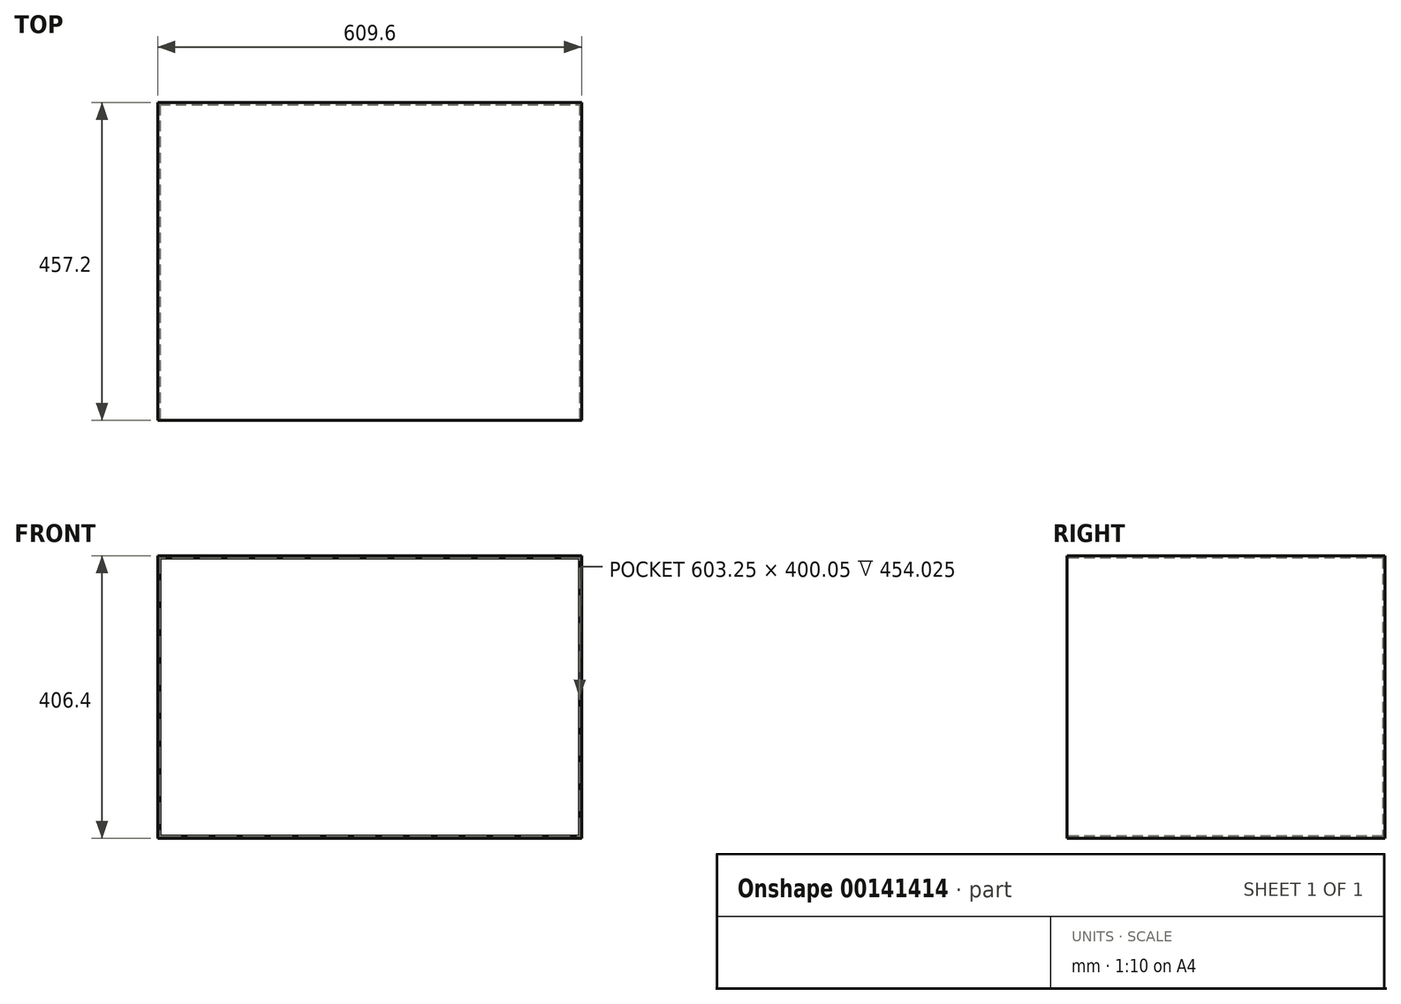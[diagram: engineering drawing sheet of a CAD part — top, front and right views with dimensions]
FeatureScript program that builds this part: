
annotation { "Feature Type Name" : "Feature", "Feature Type Description" : "" }
export const myFeature = defineFeature(function(context is Context, id is Id, definition is map)
    precondition{}
    {
        {
            var Q0;
            Q0=qCreatedBy(makeId("Top.planeOp"),FACE);
            var sketch = newSketch(context, id + "F0", { "sketchPlane" : qUnion([Q0])});
            skLineSegment(sketch, "E0.bottom", {"start": v(-304.8, 228.6) * mm, "end": v(304.8, 228.6) * mm});
            skLineSegment(sketch, "E0.top", {"start": v(-304.8, -228.6) * mm, "end": v(304.8, -228.6) * mm});
            skLineSegment(sketch, "E0.left", {"start": v(-304.8, 228.6) * mm, "end": v(-304.8, -228.6) * mm});
            skLineSegment(sketch, "E0.right", {"start": v(304.8, 228.6) * mm, "end": v(304.8, -228.6) * mm});
            skPoint(sketch, "E0.middle", {"position": v(0, 0) * mm});
            skSolve(sketch);
        }
        {
            var Q0;
            Q0 = qSketchRegion(id + "F0", true);
            extrude(context, id + "F1", {"entities" : qUnion([Q0]), "depth" : 406.4 * mm});
        }
        {
            var Q0;
            Q0=makeQuery(id+"F1.opExtrude","SWEPT_FACE",FACE,{"disambiguationData":[OSD([sQuery(id+"F0.wireOp",EDGE,"E0.top")])]});
            var sketch = newSketch(context, id + "F2", { "sketchPlane" : qUnion([Q0])});
            skLineSegment(sketch, "E1.bottom", {"start": v(-301.63, 403.23) * mm, "end": v(301.63, 403.23) * mm});
            skLineSegment(sketch, "E1.top", {"start": v(-301.63, 3.18) * mm, "end": v(301.63, 3.18) * mm});
            skLineSegment(sketch, "E1.left", {"start": v(-301.63, 403.23) * mm, "end": v(-301.63, 3.18) * mm});
            skLineSegment(sketch, "E1.right", {"start": v(301.63, 403.23) * mm, "end": v(301.63, 3.18) * mm});
            skSolve(sketch);
        }
        {
            var Q0;
            Q0 = qSketchRegion(id + "F2", true);
            extrude(context, id + "F3", {"entities" : qUnion([Q0]), "operationType" : NewBodyOperationType.REMOVE, "oppositeDirection" : true, "depth" : 454.02 * mm});
        }
    });
